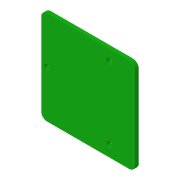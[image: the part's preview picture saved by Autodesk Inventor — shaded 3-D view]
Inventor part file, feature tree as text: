
AUTODESK INVENTOR PART (.ipt)
format: ipt  version: 2018 (Build 220112000, 112)  size: 109,056 bytes
history: native  units: in
note: dims shown in document units (in); Inventor stores cm internally (conversion verified against a paired STEP export)
features: extrude x2, sketch x2, fillet x1
ambient origin geometry x8: Origin, YZ Plane, XZ Plane, XY Plane, X Axis, Y Axis, Z Axis, Center Point
bodies: Solid1 (feature_tree)
feature tree (5):
  extrude  "Extrusion1"  Depth=2.0in
  fillet  "Fillet1"  Radius=2.0in
  extrude  "Extrusion2"  Depth=0.0787in TaperAngle=0.0deg
  sketch  "Sketch1"  dims[d0=1.0in d1=2.0in d2=2.0in]
  sketch  "Sketch2"  dims[d3=1.0in d4=0.0787in d5=0.0in d6=0.125in d7=0.1181in d9=0.1181in d15=0.0787in d16=0.0in d17=0.1181in d18=0.2362in d19=0.2362in d20=0.5512in d21=0.5512in d22=0.1181in]
